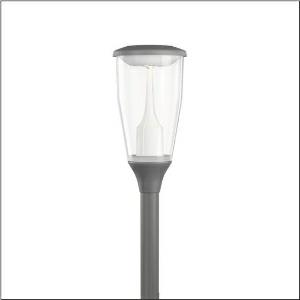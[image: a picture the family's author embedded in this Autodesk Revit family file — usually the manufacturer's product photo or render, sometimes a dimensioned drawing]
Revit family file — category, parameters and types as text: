
# Revit family: dl_11_iq___p1_0a_5xa5575lf14h000022_ea02
name_source: partatom
category: Lighting Fixtures
units: mm (PartAtom-declared; Revit-internal decimal feet)

## family parameters
Cut with Voids When Loaded = No
Host = Face
Light Source = No
Part Type = Normal
Room Calculation Point = No
Round Connector Dimension = Use Diameter
Shared = No

## types (1)
- --- (1 x LED, 1530 lm, 10 W, 4000K)
    Apparent Load = 10 VA
    CIE Flux Codes = 34 63 91 95 100
    Color Rendering = 70
    Color Temperature = 4000K
    Default Elevation = 1800 mm
    Description = DL 11 iQ, mast luminaire, Module 540 iQ-SR, primary light control with 3 zone facetted reflector, of plastic, silver coated, highly specular, structured, primary optical cover: cover, of PMMA, transparent, light distribution: P1.0a, light emission: direct distribution, primary light characteristic: asymmetric, installation type: post-top, LED, High Power LED, light colour: 740, colour temperature: 4000K, control gear: iQ Street-Remote, control: Street-Remote, Auto-Match, Temp-Guard, Lumen-Switch, Night-Set, Smart-Wire, Light-Fading, Desk-Remote (wireless, voltage-free reading and setting of iQ features in the workshop via application-optimized NFC function/RFID function), optimised constant luminous flux control (CLO 2.0), mains connection: 220..240V, AC, 50/60Hz, connection cable pre-assembled, cable length: 5,5m, start of lifetime: 10W, end of service life: 10W, luminaire housing, upper part, of diecast aluminium, coated, Siteco® metallic grey (DB 702S), spigot size: 76mm (post-top), mounting height: 3..5m, post-top mast mounting element, of diecast aluminium, coated, Siteco® metallic grey (DB 702S), Module 540 iQ-SR, traffic white (RAL 9016), equipment: standard, protection rating (complete): IP66, insulation class (complete): insulation class II (safety insulation), certification: CE, ENEC, ENEC+, VDE, impact resistance: IK07, packaging unit: 1 piece

Light Distribution: P1.0a
    Height = 665 mm
    Lamp = 1 x LED
    Lamp Light Flux = 1530 lm
    Lamp Power = 10 W
    Lamp count = 1
    Length = 334 mm
    Luminous efficacy = 153 lm/W
    Manufacturer = Siteco
    ModVariant = No
    Model = 5XA5575LF14H000022
    Number of Poles = 1
    OnlyDefault = Yes
    Power Factor = 1
    Product Name = DL 11 iQ | P1.0a
    Product group = mast luminaire | pylon top
    ProductGroupID = 6100
    Protection Class = Protection class II
    Protection Degree = IP 66
    RLX_Detail_Level = 1
    RLX_Emergency_Light_Flux = 0 lm
    RLX_Emergency_Type = 0
    RLX_Emergency_Type_DB = No
    RlxData = <blob elided: 108777 chars, md5=f1deee1a>
    Socket = socket
    Standby Power = 0 W
    System Light Flux = 1530 lm
    System Power = 10 W
    Type Comments = factory setting: luminous flux: 100 % | dim-lin: 254 | 401 mA
    Type Image = l_1258354.jpg
    URL = http://relux.com
    VarID = @adj_113249
    Voltage = 0 V
    Weight = 0.00 kg
    Width = 0 mm  [stored 0 ft]

note: [stored X ft] marks values corroborated as IEEE doubles in the binary element streams (Revit-internal decimal feet)

## geometry (parser evidence)
native form markers: Blend x4, Sweep x11
no freeform markers — native parametric forms only
